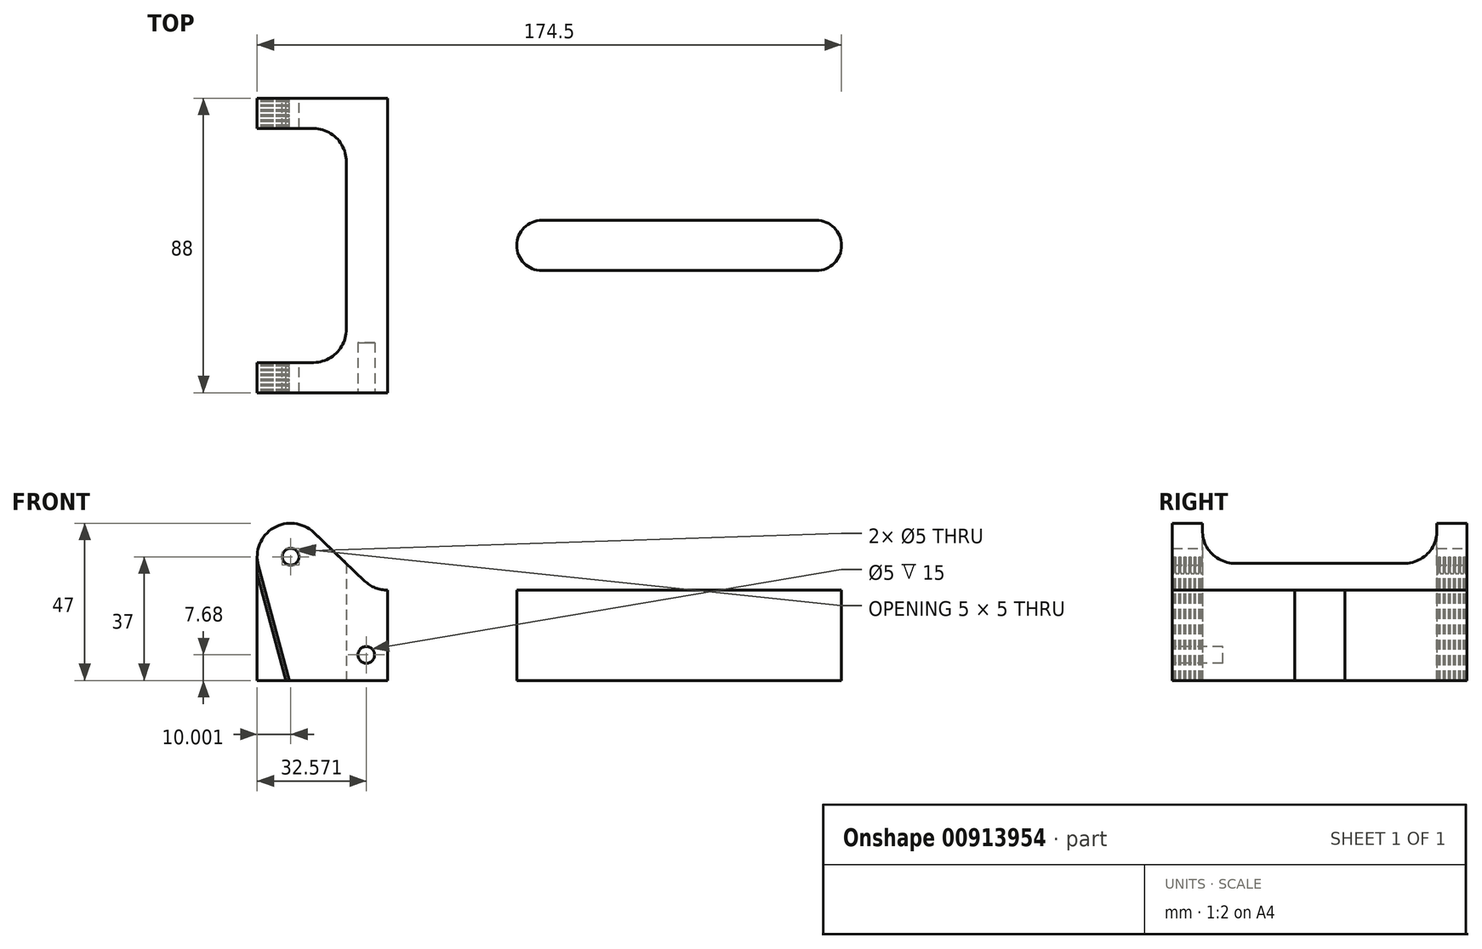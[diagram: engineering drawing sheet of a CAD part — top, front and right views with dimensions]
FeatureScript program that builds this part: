
annotation { "Feature Type Name" : "Feature", "Feature Type Description" : "" }
export const myFeature = defineFeature(function(context is Context, id is Id, definition is map)
    precondition{}
    {
        {
            var Q0;
            Q0=qCreatedBy(makeId("Front.planeOp"),FACE);
            var sketch = newSketch(context, id + "F0", { "sketchPlane" : qUnion([Q0])});
            skLineSegment(sketch, "E0", {"start": v(-26.1, 0) * mm, "end": v(161.33, 0) * mm});
            skLineSegment(sketch, "E1", {"start": v(161.33, 0) * mm, "end": v(161.33, 27) * mm});
            skLineSegment(sketch, "E2", {"start": v(161.33, 27) * mm, "end": v(-0.67, 27) * mm});
            skLineSegment(sketch, "E3", {"start": v(-26.1, 0) * mm, "end": v(-35.33, 34.41) * mm});
            skArc(sketch, "E4", {"start": v(-35.33, 34.41) * mm, "mid": v(-30.77, 45.6) * mm, "end": v(-18.77, 44.24) * mm});
            skCircle(sketch, "E5", {"center": v(-25.67, 37) * mm, "radius": 2.5 * mm});
            skLineSegment(sketch, "E6", {"start": v(-35.67, 53.82) * mm, "end": v(-35.67, 18.8) * mm, "construction": true});
            skLineSegment(sketch, "E7", {"start": v(-0.67, 27) * mm, "end": v(-18.77, 44.24) * mm});
            skSolve(sketch);
        }
        {
            var Q0;
            Q0=makeQuery(id+"F0.imprint","IMPRINT",FACE,{"disambiguationData":[TD([[makeQuery(id+"F0.imprint","IMPRINT",EDGE,{"derivedFrom":sQuery(id+"F0.wireOp",EDGE,"E0")}),1.0]])]});
            extrude(context, id + "F1", {"entities" : qUnion([Q0]), "endBound" : BoundingType.SYMMETRIC, "depth" : 88 * mm, "offsetDistance" : 25 * mm});
        }
        {
            var Q0;
            Q0=qCreatedBy(makeId("Top.planeOp"),FACE);
            var sketch = newSketch(context, id + "F2", { "sketchPlane" : qUnion([Q0])});
            skLineSegment(sketch, "E8.0", {"start": v(-35.67, 44) * mm, "end": v(-35.67, 44) * mm});
            skLineSegment(sketch, "E8.1", {"start": v(-35.67, -44) * mm, "end": v(-35.67, -44) * mm});
            skLineSegment(sketch, "E8.2", {"start": v(161.33, -44) * mm, "end": v(161.33, 44) * mm});
            skLineSegment(sketch, "E9", {"start": v(-35.67, 44) * mm, "end": v(-35.67, 35) * mm, "construction": true});
            skLineSegment(sketch, "E10", {"start": v(-35.67, 35) * mm, "end": v(-19.04, 35) * mm});
            skLineSegment(sketch, "E11", {"start": v(-35.67, -44) * mm, "end": v(-35.67, -35) * mm, "construction": true});
            skLineSegment(sketch, "E12", {"start": v(-35.67, -35) * mm, "end": v(-19.04, -35) * mm});
            skLineSegment(sketch, "E13", {"start": v(-9.04, 25) * mm, "end": v(-9.04, -25) * mm});
            skArc(sketch, "E14", {"start": v(-19.04, 35) * mm, "mid": v(-11.97, 32.07) * mm, "end": v(-9.04, 25) * mm});
            skArc(sketch, "E15", {"start": v(-19.04, -35) * mm, "mid": v(-11.97, -32.07) * mm, "end": v(-9.04, -25) * mm});
            skLineSegment(sketch, "E16", {"start": v(-35.67, 35) * mm, "end": v(-35.67, -35) * mm});
            skLineSegment(sketch, "E17", {"start": v(161.33, 13.5) * mm, "end": v(18.6, 13.5) * mm});
            skLineSegment(sketch, "E18", {"start": v(161.33, -13.5) * mm, "end": v(18.6, -13.5) * mm});
            skLineSegment(sketch, "E19", {"start": v(0, 0) * mm, "end": v(18.6, 13.5) * mm, "construction": true});
            skLineSegment(sketch, "E20", {"start": v(0, 0) * mm, "end": v(18.6, -13.5) * mm, "construction": true});
            skLineSegment(sketch, "E21", {"start": v(4.33, 44) * mm, "end": v(8.8, 21.55) * mm});
            skLineSegment(sketch, "E22", {"start": v(4.33, -44) * mm, "end": v(8.8, -21.55) * mm});
            skArc(sketch, "E23", {"start": v(8.8, 21.55) * mm, "mid": v(12.26, 15.77) * mm, "end": v(18.6, 13.5) * mm});
            skArc(sketch, "E24", {"start": v(8.8, -21.55) * mm, "mid": v(12.26, -15.77) * mm, "end": v(18.6, -13.5) * mm});
            skLineSegment(sketch, "E25", {"start": v(4.33, 44) * mm, "end": v(161.33, 44) * mm});
            skLineSegment(sketch, "E26", {"start": v(4.33, -44) * mm, "end": v(161.33, -44) * mm});
            skLineSegment(sketch, "E27.0", {"start": v(-0.67, -44) * mm, "end": v(-0.67, 44) * mm});
            skSolve(sketch);
        }
        {
            var Q0;
            Q0=makeQuery(id+"F2.imprint","IMPRINT",FACE,{"disambiguationData":[TD([[makeQuery(id+"F2.imprint","IMPRINT",EDGE,{"derivedFrom":sQuery(id+"F2.wireOp",EDGE,"E10")}),-1.0]])]});
            var Q1;
            {var subQ2=sQuery(id+"F2.wireOp",EDGE,"E17");Q1=makeQuery(id+"F2.imprint","IMPRINT",FACE,{"disambiguationData":[TD([[makeQuery(id+"F2.imprint","IMPRINT",EDGE,{"derivedFrom":subQ2}),-1.0]])]});}
            var Q2;
            {var subQ2=sQuery(id+"F2.wireOp",EDGE,"E18");Q2=makeQuery(id+"F2.imprint","IMPRINT",FACE,{"disambiguationData":[TD([[makeQuery(id+"F2.imprint","IMPRINT",EDGE,{"derivedFrom":subQ2}),1.0]])]});}
            var Q3;
            Q3=makeQuery(id+"F1.opExtrude","SWEPT_FACE",FACE,{"disambiguationData":[OSD([sQuery(id+"F0.wireOp",EDGE,"4be1d8de-59d6-4cd1-a754-1055a2beaf2e")])]});
            var Q4;
            Q4=makeQuery(id+"F1.opExtrude","SWEPT_FACE",FACE,{"disambiguationData":[OSD([sQuery(id+"F0.wireOp",EDGE,"E0")])]});
            extrude(context, id + "F3", {"entities" : qUnion([Q0, Q1, Q2]), "operationType" : NewBodyOperationType.REMOVE, "endBound" : BoundingType.THROUGH_ALL, "depth" : 25 * mm, "endBoundEntityFace" : qUnion([Q3]), "offsetDistance" : 25 * mm});
        }
        {
            var Q0;
            Q0=makeQuery(id+"F1.opExtrude","CAP_FACE",FACE,{"disambiguationData":[OSD([sQuery(id+"F0.wireOp",EDGE,"E0"),sQuery(id+"F0.wireOp",EDGE,"E1"),sQuery(id+"F0.wireOp",EDGE,"E2"),sQuery(id+"F0.wireOp",EDGE,"4gLOaJfr-lTau-UGmt-n1u9-BmUXGN7Fvg1A"),sQuery(id+"F0.wireOp",EDGE,"ggTN4X47-m9Sh-A01e-3FZt-2B0qIQw0AuEr"),sQuery(id+"F0.wireOp",EDGE,"E3"),sQuery(id+"F0.wireOp",EDGE,"E4"),sQuery(id+"F0.wireOp",EDGE,"4be1d8de-59d6-4cd1-a754-1055a2beaf2e"),sQuery(id+"F0.wireOp",EDGE,"E5")])],"isStart":false});
            var sketch = newSketch(context, id + "F4", { "sketchPlane" : qUnion([Q0])});
            skCircle(sketch, "E28.0", {"center": v(-25.67, 37) * mm, "radius": 2.5 * mm});
            skCircle(sketch, "E29", {"center": v(-3.1, 7.68) * mm, "radius": 2.5 * mm});
            skCircle(sketch, "E30", {"center": v(29.33, 13.5) * mm, "radius": 2.5 * mm});
            skCircle(sketch, "E31", {"center": v(151.33, 13.5) * mm, "radius": 2.5 * mm});
            skSolve(sketch);
        }
        {
            var Q0;
            Q0=makeQuery(id+"F4.imprint","IMPRINT",FACE,{"disambiguationData":[TD([[makeQuery(id+"F4.imprint","IMPRINT",EDGE,{"derivedFrom":sQuery(id+"F4.wireOp",EDGE,"E30")}),1.0]])]});
            var Q1;
            Q1=makeQuery(id+"F4.imprint","IMPRINT",FACE,{"disambiguationData":[TD([[makeQuery(id+"F4.imprint","IMPRINT",EDGE,{"derivedFrom":sQuery(id+"F4.wireOp",EDGE,"E31")}),1.0]])]});
            var Q2;
            Q2=makeQuery(id+"F3.boolean.opBoolean","COPY",FACE,{"derivedFrom":makeQuery(id+"F3.opExtrude","SWEPT_FACE",FACE,{"disambiguationData":[OSD([sQuery(id+"F2.wireOp",EDGE,"E17")])]})});
            extrude(context, id + "F5", {"entities" : qUnion([Q0, Q1]), "operationType" : NewBodyOperationType.REMOVE, "endBound" : BoundingType.UP_TO_SURFACE, "oppositeDirection" : true, "depth" : 25 * mm, "endBoundEntityFace" : qUnion([Q2]), "offsetDistance" : 25 * mm});
        }
        {
            var Q0;
            Q0=makeQuery(id+"F4.imprint","IMPRINT",FACE,{"disambiguationData":[TD([[makeQuery(id+"F4.imprint","IMPRINT",EDGE,{"derivedFrom":sQuery(id+"F4.wireOp",EDGE,"E29")}),1.0]])]});
            var Q1;
            Q1=makeQuery(id+"F1.opExtrude","CAP_FACE",FACE,{"disambiguationData":[OSD([sQuery(id+"F0.wireOp",EDGE,"E0"),sQuery(id+"F0.wireOp",EDGE,"E1"),sQuery(id+"F0.wireOp",EDGE,"E2"),sQuery(id+"F0.wireOp",EDGE,"4gLOaJfr-lTau-UGmt-n1u9-BmUXGN7Fvg1A"),sQuery(id+"F0.wireOp",EDGE,"ggTN4X47-m9Sh-A01e-3FZt-2B0qIQw0AuEr"),sQuery(id+"F0.wireOp",EDGE,"E3"),sQuery(id+"F0.wireOp",EDGE,"E4"),sQuery(id+"F0.wireOp",EDGE,"4be1d8de-59d6-4cd1-a754-1055a2beaf2e"),sQuery(id+"F0.wireOp",EDGE,"E5")])],"isStart":true});
            extrude(context, id + "F6", {"entities" : qUnion([Q0]), "operationType" : NewBodyOperationType.REMOVE, "oppositeDirection" : true, "depth" : 15 * mm, "endBoundEntityFace" : qUnion([Q1]), "offsetDistance" : 25 * mm});
        }
        {
            var Q0;
            Q0=makeQuery(id+"F1.opExtrude","SWEPT_EDGE",EDGE,{"disambiguationData":[OSD([sQuery(id+"F0.wireOp",EDGE,"E2"),sQuery(id+"F0.wireOp",EDGE,"E7")])]});
            fillet(context, id + "F7", {"entities" : qUnion([Q0]), "radius" : 10 * mm, "tangentPropagation" : true, "allowEdgeOverflow" : false});
        }
        {
            var Q0;
            Q0=makeQuery(id+"F1.opExtrude","SWEPT_FACE",FACE,{"disambiguationData":[OSD([sQuery(id+"F0.wireOp",EDGE,"E0")])]});
            var sketch = newSketch(context, id + "F8", { "sketchPlane" : qUnion([Q0])});
            skLineSegment(sketch, "E32.0", {"start": v(-19.04, 35) * mm, "end": v(-35.67, 35) * mm});
            skLineSegment(sketch, "E32.1", {"start": v(-35.67, 44) * mm, "end": v(-18.77, 44) * mm});
            skLineSegment(sketch, "E32.2", {"start": v(-19.04, -35) * mm, "end": v(-35.67, -35) * mm});
            skLineSegment(sketch, "E32.3", {"start": v(-35.67, -44) * mm, "end": v(-18.77, -44) * mm});
            skLineSegment(sketch, "E32.4", {"start": v(-26.1, -35) * mm, "end": v(-26.1, -44) * mm});
            skLineSegment(sketch, "E32.5", {"start": v(-26.1, 44) * mm, "end": v(-26.1, 35) * mm});
            skLineSegment(sketch, "E32.6", {"start": v(-35.33, 44) * mm, "end": v(-35.33, 35) * mm});
            skLineSegment(sketch, "E32.7", {"start": v(-35.33, -35) * mm, "end": v(-35.33, -44) * mm});
            skLineSegment(sketch, "E33", {"start": v(-35.67, 35) * mm, "end": v(-35.67, 44) * mm});
            skLineSegment(sketch, "E34", {"start": v(-35.67, -44) * mm, "end": v(-35.67, -35) * mm});
            skSolve(sketch);
        }
        {
            var Q0;
            {var subQ0=sQuery(id+"F8.wireOp",EDGE,"E32.5");Q0=makeQuery(id+"F8.imprint","IMPRINT",FACE,{"disambiguationData":[TD([[makeQuery(id+"F8.imprint","IMPRINT",EDGE,{"derivedFrom":subQ0}),-1.0]])]});}
            var Q1;
            {var subQ2=sQuery(id+"F8.wireOp",EDGE,"E32.6");Q1=makeQuery(id+"F8.imprint","IMPRINT",FACE,{"disambiguationData":[TD([[makeQuery(id+"F8.imprint","IMPRINT",EDGE,{"derivedFrom":subQ2}),-1.0]])]});}
            var Q2;
            {var subQ0=sQuery(id+"F8.wireOp",EDGE,"E32.4");Q2=makeQuery(id+"F8.imprint","IMPRINT",FACE,{"disambiguationData":[TD([[makeQuery(id+"F8.imprint","IMPRINT",EDGE,{"derivedFrom":subQ0}),-1.0]])]});}
            var Q3;
            {var subQ2=sQuery(id+"F8.wireOp",EDGE,"E32.7");Q3=makeQuery(id+"F8.imprint","IMPRINT",FACE,{"disambiguationData":[TD([[makeQuery(id+"F8.imprint","IMPRINT",EDGE,{"derivedFrom":subQ2}),-1.0]])]});}
            var Q4;
            Q4=makeQuery(id+"F1.opExtrude","SWEPT_BODY",BODY,{"disambiguationData":[OSD([sQuery(id+"F0.wireOp",EDGE,"E0"),sQuery(id+"F0.wireOp",EDGE,"E1"),sQuery(id+"F0.wireOp",EDGE,"E2"),sQuery(id+"F0.wireOp",EDGE,"4gLOaJfr-lTau-UGmt-n1u9-BmUXGN7Fvg1A"),sQuery(id+"F0.wireOp",EDGE,"ggTN4X47-m9Sh-A01e-3FZt-2B0qIQw0AuEr"),sQuery(id+"F0.wireOp",EDGE,"E3"),sQuery(id+"F0.wireOp",EDGE,"E4"),sQuery(id+"F0.wireOp",EDGE,"4be1d8de-59d6-4cd1-a754-1055a2beaf2e"),sQuery(id+"F0.wireOp",EDGE,"E5")])]});
            extrude(context, id + "F9", {"entities" : qUnion([Q0, Q1, Q2, Q3]), "endBound" : BoundingType.UP_TO_BODY, "oppositeDirection" : true, "depth" : 25 * mm, "endBoundEntityBody" : qUnion([Q4]), "offsetDistance" : 25 * mm});
        }
        {
            var Q0;
            Q0=makeQuery(id+"F1.opExtrude","SWEPT_FACE",FACE,{"disambiguationData":[OSD([sQuery(id+"F0.wireOp",EDGE,"E2")])]});
            var sketch = newSketch(context, id + "F10", { "sketchPlane" : qUnion([Q0])});
            skLineSegment(sketch, "E35.0", {"start": v(31.83, -13.5) * mm, "end": v(26.83, -13.5) * mm});
            skLineSegment(sketch, "E35.1", {"start": v(153.83, -13.5) * mm, "end": v(148.83, -13.5) * mm});
            skLineSegment(sketch, "E36.0", {"start": v(148.83, 13.5) * mm, "end": v(153.83, 13.5) * mm});
            skLineSegment(sketch, "E36.1", {"start": v(26.83, 13.5) * mm, "end": v(31.83, 13.5) * mm});
            skLineSegment(sketch, "E37", {"start": v(31.83, 13.5) * mm, "end": v(31.83, -13.5) * mm, "construction": true});
            skLineSegment(sketch, "E38", {"start": v(148.83, 13.5) * mm, "end": v(148.83, -13.5) * mm, "construction": true});
            skLineSegment(sketch, "E39", {"start": v(31.83, 0) * mm, "end": v(49.33, 0) * mm, "construction": true});
            skLineSegment(sketch, "E40", {"start": v(148.83, 0) * mm, "end": v(131.33, 0) * mm, "construction": true});
            skArc(sketch, "E41", {"start": v(49.33, -7.5) * mm, "mid": v(41.83, 0) * mm, "end": v(49.33, 7.5) * mm});
            skArc(sketch, "E42", {"start": v(131.33, -7.5) * mm, "mid": v(138.83, 0) * mm, "end": v(131.33, 7.5) * mm});
            skLineSegment(sketch, "E43", {"start": v(49.33, 7.5) * mm, "end": v(131.33, 7.5) * mm});
            skLineSegment(sketch, "E44", {"start": v(49.33, -7.5) * mm, "end": v(131.33, -7.5) * mm});
            skSolve(sketch);
        }
        {
            var Q0;
            Q0=makeQuery(id+"F10.imprint","IMPRINT",FACE,{"disambiguationData":[TD([[makeQuery(id+"F10.imprint","IMPRINT",EDGE,{"derivedFrom":sQuery(id+"F10.wireOp",EDGE,"E41")}),-1.0]])]});
            var Q1;
            Q1=makeQuery(id+"F1.opExtrude","SWEPT_FACE",FACE,{"disambiguationData":[OSD([sQuery(id+"F0.wireOp",EDGE,"E0")])]});
            extrude(context, id + "F11", {"entities" : qUnion([Q0]), "operationType" : NewBodyOperationType.REMOVE, "endBound" : BoundingType.UP_TO_SURFACE, "oppositeDirection" : true, "depth" : 25 * mm, "endBoundEntityFace" : qUnion([Q1]), "offsetDistance" : 25 * mm});
        }
        {
            var Q0;
            {var subQ2=sQuery(id+"F8.wireOp",EDGE,"E32.4");Q0=makeQuery(id+"F8.imprint","IMPRINT",FACE,{"disambiguationData":[TD([[makeQuery(id+"F8.imprint","IMPRINT",EDGE,{"derivedFrom":subQ2}),1.0]])]});}
            var sketch = newSketch(context, id + "F12", { "sketchPlane" : qUnion([Q0])});
            skPoint(sketch, "E45.0", {"position": v(-26.1, 44) * mm});
            skPoint(sketch, "E45.1", {"position": v(-26.1, 35) * mm});
            skPoint(sketch, "E45.2", {"position": v(-26.1, -35) * mm});
            skPoint(sketch, "E45.3", {"position": v(-26.1, -44) * mm});
            skLineSegment(sketch, "E46", {"start": v(-27.1, 44) * mm, "end": v(-27.1, 43.5) * mm});
            skLineSegment(sketch, "E47", {"start": v(-27.1, 43.5) * mm, "end": v(-26.1, 43.5) * mm});
            skLineSegment(sketch, "E48", {"start": v(-26.1, 43.5) * mm, "end": v(-26.1, 43) * mm});
            skLineSegment(sketch, "E49", {"start": v(-26.1, 43) * mm, "end": v(-27.1, 43) * mm});
            skLineSegment(sketch, "E50", {"start": v(-27.1, 43) * mm, "end": v(-27.1, 42.5) * mm});
            skLineSegment(sketch, "E51.0.1.0", {"start": v(-27.1, 42.5) * mm, "end": v(-27.1, 42) * mm});
            skLineSegment(sketch, "E51.0.1.1", {"start": v(-27.1, 42) * mm, "end": v(-26.1, 42) * mm});
            skLineSegment(sketch, "E51.0.1.2", {"start": v(-26.1, 42) * mm, "end": v(-26.1, 41.5) * mm});
            skLineSegment(sketch, "E51.0.1.3", {"start": v(-26.1, 41.5) * mm, "end": v(-27.1, 41.5) * mm});
            skLineSegment(sketch, "E51.0.1.4", {"start": v(-27.1, 41.5) * mm, "end": v(-27.1, 41) * mm});
            skLineSegment(sketch, "E51.0.2.0", {"start": v(-27.1, 41) * mm, "end": v(-27.1, 40.5) * mm});
            skLineSegment(sketch, "E51.0.2.1", {"start": v(-27.1, 40.5) * mm, "end": v(-26.1, 40.5) * mm});
            skLineSegment(sketch, "E51.0.2.2", {"start": v(-26.1, 40.5) * mm, "end": v(-26.1, 40) * mm});
            skLineSegment(sketch, "E51.0.2.3", {"start": v(-26.1, 40) * mm, "end": v(-27.1, 40) * mm});
            skLineSegment(sketch, "E51.0.2.4", {"start": v(-27.1, 40) * mm, "end": v(-27.1, 39.5) * mm});
            skLineSegment(sketch, "E51.0.3.0", {"start": v(-27.1, 39.5) * mm, "end": v(-27.1, 39) * mm});
            skLineSegment(sketch, "E51.0.3.1", {"start": v(-27.1, 39) * mm, "end": v(-26.1, 39) * mm});
            skLineSegment(sketch, "E51.0.3.2", {"start": v(-26.1, 39) * mm, "end": v(-26.1, 38.5) * mm});
            skLineSegment(sketch, "E51.0.3.3", {"start": v(-26.1, 38.5) * mm, "end": v(-27.1, 38.5) * mm});
            skLineSegment(sketch, "E51.0.3.4", {"start": v(-27.1, 38.5) * mm, "end": v(-27.1, 38) * mm});
            skLineSegment(sketch, "E51.0.4.0", {"start": v(-27.1, 38) * mm, "end": v(-27.1, 37.5) * mm});
            skLineSegment(sketch, "E51.0.4.1", {"start": v(-27.1, 37.5) * mm, "end": v(-26.1, 37.5) * mm});
            skLineSegment(sketch, "E51.0.4.2", {"start": v(-26.1, 37.5) * mm, "end": v(-26.1, 37) * mm});
            skLineSegment(sketch, "E51.0.4.3", {"start": v(-26.1, 37) * mm, "end": v(-27.1, 37) * mm});
            skLineSegment(sketch, "E51.0.4.4", {"start": v(-27.1, 37) * mm, "end": v(-27.1, 36.5) * mm});
            skLineSegment(sketch, "E51.0.5.0", {"start": v(-27.1, 36.5) * mm, "end": v(-27.1, 36) * mm});
            skLineSegment(sketch, "E51.0.5.1", {"start": v(-27.1, 36) * mm, "end": v(-26.1, 36) * mm});
            skLineSegment(sketch, "E51.0.5.2", {"start": v(-26.1, 36) * mm, "end": v(-26.1, 35.5) * mm});
            skLineSegment(sketch, "E51.0.5.3", {"start": v(-26.1, 35.5) * mm, "end": v(-27.1, 35.5) * mm});
            skLineSegment(sketch, "E51.0.5.4", {"start": v(-27.1, 35.5) * mm, "end": v(-27.1, 35) * mm});
            skLineSegment(sketch, "E51.direction1", {"start": v(-27.1, 42.5) * mm, "end": v(-2.1, 42.5) * mm, "construction": true});
            skLineSegment(sketch, "E51.direction2", {"start": v(-27.1, 42.5) * mm, "end": v(-27.1, 41) * mm, "construction": true});
            skLineSegment(sketch, "E52", {"start": v(-26.1, 44) * mm, "end": v(-26.1, 35) * mm});
            skLineSegment(sketch, "E53", {"start": v(-26.1, 44) * mm, "end": v(-27.1, 44) * mm});
            skLineSegment(sketch, "E54", {"start": v(-26.1, 35) * mm, "end": v(-27.1, 35) * mm});
            skLineSegment(sketch, "E55", {"start": v(-27.1, -35) * mm, "end": v(-27.1, -35.5) * mm});
            skLineSegment(sketch, "E56", {"start": v(-27.1, -35.5) * mm, "end": v(-26.1, -35.5) * mm});
            skLineSegment(sketch, "E57", {"start": v(-26.1, -35.5) * mm, "end": v(-26.1, -36) * mm});
            skLineSegment(sketch, "E58", {"start": v(-26.1, -36) * mm, "end": v(-27.1, -36) * mm});
            skLineSegment(sketch, "E59", {"start": v(-27.1, -36) * mm, "end": v(-27.1, -36.5) * mm});
            skLineSegment(sketch, "E60.0.1.0", {"start": v(-27.1, -36.5) * mm, "end": v(-27.1, -37) * mm});
            skLineSegment(sketch, "E60.0.1.1", {"start": v(-27.1, -37) * mm, "end": v(-26.1, -37) * mm});
            skLineSegment(sketch, "E60.0.1.2", {"start": v(-26.1, -37) * mm, "end": v(-26.1, -37.5) * mm});
            skLineSegment(sketch, "E60.0.1.3", {"start": v(-26.1, -37.5) * mm, "end": v(-27.1, -37.5) * mm});
            skLineSegment(sketch, "E60.0.1.4", {"start": v(-27.1, -37.5) * mm, "end": v(-27.1, -38) * mm});
            skLineSegment(sketch, "E60.0.2.0", {"start": v(-27.1, -38) * mm, "end": v(-27.1, -38.5) * mm});
            skLineSegment(sketch, "E60.0.2.1", {"start": v(-27.1, -38.5) * mm, "end": v(-26.1, -38.5) * mm});
            skLineSegment(sketch, "E60.0.2.2", {"start": v(-26.1, -38.5) * mm, "end": v(-26.1, -39) * mm});
            skLineSegment(sketch, "E60.0.2.3", {"start": v(-26.1, -39) * mm, "end": v(-27.1, -39) * mm});
            skLineSegment(sketch, "E60.0.2.4", {"start": v(-27.1, -39) * mm, "end": v(-27.1, -39.5) * mm});
            skLineSegment(sketch, "E60.0.3.0", {"start": v(-27.1, -39.5) * mm, "end": v(-27.1, -40) * mm});
            skLineSegment(sketch, "E60.0.3.1", {"start": v(-27.1, -40) * mm, "end": v(-26.1, -40) * mm});
            skLineSegment(sketch, "E60.0.3.2", {"start": v(-26.1, -40) * mm, "end": v(-26.1, -40.5) * mm});
            skLineSegment(sketch, "E60.0.3.3", {"start": v(-26.1, -40.5) * mm, "end": v(-27.1, -40.5) * mm});
            skLineSegment(sketch, "E60.0.3.4", {"start": v(-27.1, -40.5) * mm, "end": v(-27.1, -41) * mm});
            skLineSegment(sketch, "E60.0.4.0", {"start": v(-27.1, -41) * mm, "end": v(-27.1, -41.5) * mm});
            skLineSegment(sketch, "E60.0.4.1", {"start": v(-27.1, -41.5) * mm, "end": v(-26.1, -41.5) * mm});
            skLineSegment(sketch, "E60.0.4.2", {"start": v(-26.1, -41.5) * mm, "end": v(-26.1, -42) * mm});
            skLineSegment(sketch, "E60.0.4.3", {"start": v(-26.1, -42) * mm, "end": v(-27.1, -42) * mm});
            skLineSegment(sketch, "E60.0.4.4", {"start": v(-27.1, -42) * mm, "end": v(-27.1, -42.5) * mm});
            skLineSegment(sketch, "E60.0.5.0", {"start": v(-27.1, -42.5) * mm, "end": v(-27.1, -43) * mm});
            skLineSegment(sketch, "E60.0.5.1", {"start": v(-27.1, -43) * mm, "end": v(-26.1, -43) * mm});
            skLineSegment(sketch, "E60.0.5.2", {"start": v(-26.1, -43) * mm, "end": v(-26.1, -43.5) * mm});
            skLineSegment(sketch, "E60.0.5.3", {"start": v(-26.1, -43.5) * mm, "end": v(-27.1, -43.5) * mm});
            skLineSegment(sketch, "E60.0.5.4", {"start": v(-27.1, -43.5) * mm, "end": v(-27.1, -44) * mm});
            skLineSegment(sketch, "E60.direction1", {"start": v(-27.1, -36.5) * mm, "end": v(-2.1, -36.5) * mm, "construction": true});
            skLineSegment(sketch, "E60.direction2", {"start": v(-27.1, -36.5) * mm, "end": v(-27.1, -38) * mm, "construction": true});
            skLineSegment(sketch, "E61", {"start": v(-26.1, -35) * mm, "end": v(-26.1, -44) * mm});
            skLineSegment(sketch, "E62", {"start": v(-26.1, -35) * mm, "end": v(-27.1, -35) * mm});
            skLineSegment(sketch, "E63", {"start": v(-26.1, -44) * mm, "end": v(-27.1, -44) * mm});
            skSolve(sketch);
        }
        {
            var Q0;
            Q0=makeQuery(id+"F12.imprint","IMPRINT",FACE,{"disambiguationData":[TD([[makeQuery(id+"F12.imprint","IMPRINT",EDGE,{"derivedFrom":sQuery(id+"F12.wireOp",EDGE,"E46")}),1.0]])]});
            var Q1;
            {var subQ2=sQuery(id+"F12.wireOp",EDGE,"E49");Q1=makeQuery(id+"F12.imprint","IMPRINT",FACE,{"disambiguationData":[TD([[makeQuery(id+"F12.imprint","IMPRINT",EDGE,{"derivedFrom":subQ2}),1.0]])]});}
            var Q2;
            {var subQ1=sQuery(id+"F12.wireOp",EDGE,"E51.0.1.3");Q2=makeQuery(id+"F12.imprint","IMPRINT",FACE,{"disambiguationData":[TD([[makeQuery(id+"F12.imprint","IMPRINT",EDGE,{"derivedFrom":subQ1}),1.0]])]});}
            var Q3;
            {var subQ1=sQuery(id+"F12.wireOp",EDGE,"E51.0.2.3");Q3=makeQuery(id+"F12.imprint","IMPRINT",FACE,{"disambiguationData":[TD([[makeQuery(id+"F12.imprint","IMPRINT",EDGE,{"derivedFrom":subQ1}),1.0]])]});}
            var Q4;
            {var subQ1=sQuery(id+"F12.wireOp",EDGE,"E51.0.3.3");Q4=makeQuery(id+"F12.imprint","IMPRINT",FACE,{"disambiguationData":[TD([[makeQuery(id+"F12.imprint","IMPRINT",EDGE,{"derivedFrom":subQ1}),1.0]])]});}
            var Q5;
            {var subQ1=sQuery(id+"F12.wireOp",EDGE,"E51.0.4.3");Q5=makeQuery(id+"F12.imprint","IMPRINT",FACE,{"disambiguationData":[TD([[makeQuery(id+"F12.imprint","IMPRINT",EDGE,{"derivedFrom":subQ1}),1.0]])]});}
            var Q6;
            {var subQ0=sQuery(id+"F12.wireOp",EDGE,"E51.0.5.3");Q6=makeQuery(id+"F12.imprint","IMPRINT",FACE,{"disambiguationData":[TD([[makeQuery(id+"F12.imprint","IMPRINT",EDGE,{"derivedFrom":subQ0}),1.0]])]});}
            var Q7;
            {var subQ0=sQuery(id+"F0.wireOp",EDGE,"E3");Q7=makeQuery(id+"F9.opExtrude","CAP_EDGE",EDGE,{"disambiguationData":[OSD([subQ0]),TDD([makeQuery(id+"F1.opExtrude","CAP_EDGE",EDGE,{"disambiguationData":[OSD([subQ0])],"isStart":false})])],"isStart":false});}
            var Q8;
            {var subQ0=sQuery(id+"F0.wireOp",EDGE,"E4");Q8=makeQuery(id+"F9.opExtrude","CAP_EDGE",EDGE,{"disambiguationData":[OSD([subQ0]),TDD([makeQuery(id+"F1.opExtrude","CAP_EDGE",EDGE,{"disambiguationData":[OSD([subQ0])],"isStart":false})])],"isStart":false});}
            sweep(context, id + "F13", {"operationType" : NewBodyOperationType.REMOVE, "profiles" : qUnion([Q0, Q1, Q2, Q3, Q4, Q5, Q6]), "path" : qUnion([Q7, Q8])});
        }
        {
            var Q0;
            Q0=makeQuery(id+"F12.imprint","IMPRINT",FACE,{"disambiguationData":[TD([[makeQuery(id+"F12.imprint","IMPRINT",EDGE,{"derivedFrom":sQuery(id+"F12.wireOp",EDGE,"E55")}),1.0]])]});
            var Q1;
            {var subQ2=sQuery(id+"F12.wireOp",EDGE,"E58");Q1=makeQuery(id+"F12.imprint","IMPRINT",FACE,{"disambiguationData":[TD([[makeQuery(id+"F12.imprint","IMPRINT",EDGE,{"derivedFrom":subQ2}),1.0]])]});}
            var Q2;
            {var subQ1=sQuery(id+"F12.wireOp",EDGE,"E60.0.1.3");Q2=makeQuery(id+"F12.imprint","IMPRINT",FACE,{"disambiguationData":[TD([[makeQuery(id+"F12.imprint","IMPRINT",EDGE,{"derivedFrom":subQ1}),1.0]])]});}
            var Q3;
            {var subQ1=sQuery(id+"F12.wireOp",EDGE,"E60.0.2.3");Q3=makeQuery(id+"F12.imprint","IMPRINT",FACE,{"disambiguationData":[TD([[makeQuery(id+"F12.imprint","IMPRINT",EDGE,{"derivedFrom":subQ1}),1.0]])]});}
            var Q4;
            {var subQ1=sQuery(id+"F12.wireOp",EDGE,"E60.0.3.3");Q4=makeQuery(id+"F12.imprint","IMPRINT",FACE,{"disambiguationData":[TD([[makeQuery(id+"F12.imprint","IMPRINT",EDGE,{"derivedFrom":subQ1}),1.0]])]});}
            var Q5;
            {var subQ1=sQuery(id+"F12.wireOp",EDGE,"E60.0.4.3");Q5=makeQuery(id+"F12.imprint","IMPRINT",FACE,{"disambiguationData":[TD([[makeQuery(id+"F12.imprint","IMPRINT",EDGE,{"derivedFrom":subQ1}),1.0]])]});}
            var Q6;
            {var subQ0=sQuery(id+"F12.wireOp",EDGE,"E60.0.5.3");Q6=makeQuery(id+"F12.imprint","IMPRINT",FACE,{"disambiguationData":[TD([[makeQuery(id+"F12.imprint","IMPRINT",EDGE,{"derivedFrom":subQ0}),1.0]])]});}
            var Q7;
            Q7=makeQuery(id+"F9.opExtrude","CAP_EDGE",EDGE,{"disambiguationData":[OSD([sQuery(id+"F0.wireOp",EDGE,"E3"),sQuery(id+"F2.wireOp",EDGE,"E10")])],"isStart":false});
            var Q8;
            Q8=makeQuery(id+"F9.opExtrude","CAP_EDGE",EDGE,{"disambiguationData":[OSD([sQuery(id+"F0.wireOp",EDGE,"E4"),sQuery(id+"F2.wireOp",EDGE,"E10")])],"isStart":false});
            sweep(context, id + "F14", {"operationType" : NewBodyOperationType.REMOVE, "profiles" : qUnion([Q0, Q1, Q2, Q3, Q4, Q5, Q6]), "path" : qUnion([Q7, Q8])});
        }
    });
